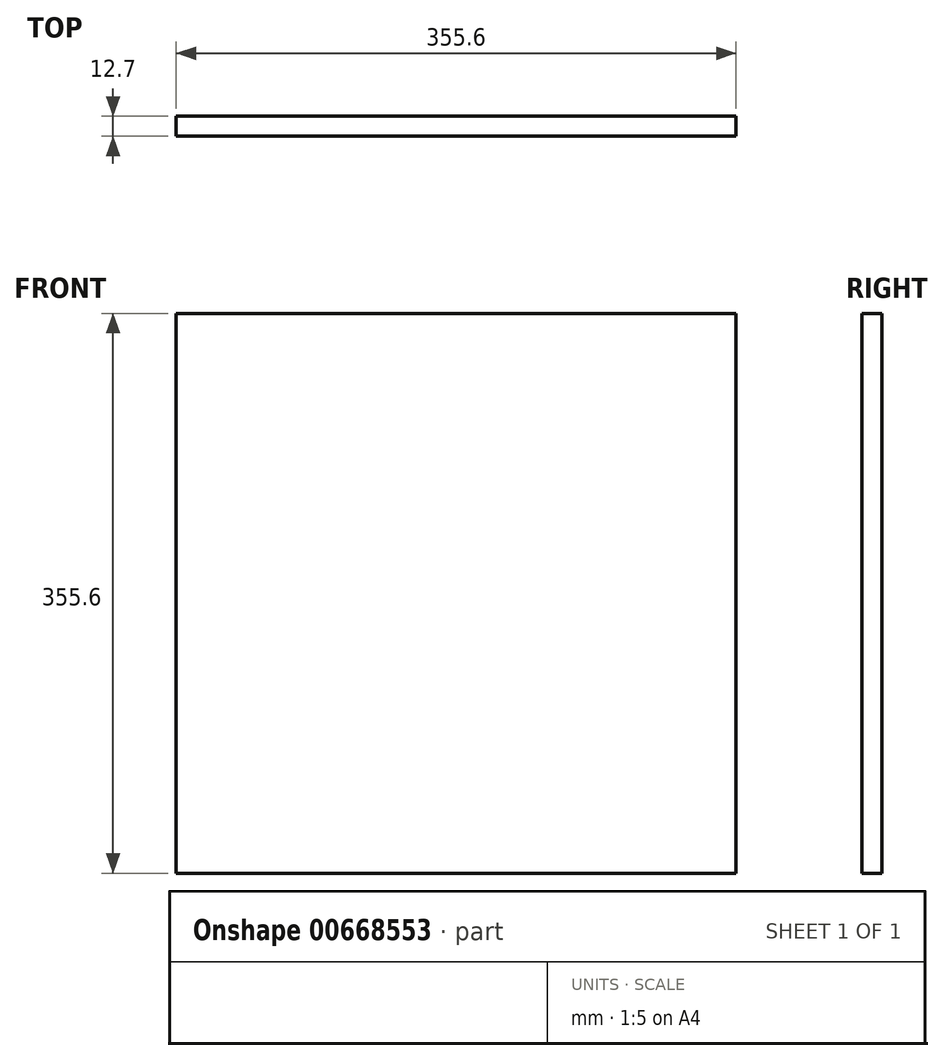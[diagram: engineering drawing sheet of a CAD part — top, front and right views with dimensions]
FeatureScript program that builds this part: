
annotation { "Feature Type Name" : "Feature", "Feature Type Description" : "" }
export const myFeature = defineFeature(function(context is Context, id is Id, definition is map)
    precondition{}
    {
        {
            var Q0;
            Q0=qCreatedBy(makeId("Front.planeOp"),FACE);
            var sketch = newSketch(context, id + "F0", { "sketchPlane" : qUnion([Q0])});
            skLineSegment(sketch, "E0.bottom", {"start": v(180, 177.8) * mm, "end": v(-175.6, 177.8) * mm});
            skLineSegment(sketch, "E0.top", {"start": v(180, -177.8) * mm, "end": v(-175.6, -177.8) * mm});
            skLineSegment(sketch, "E0.left", {"start": v(180, 177.8) * mm, "end": v(180, -177.8) * mm});
            skLineSegment(sketch, "E0.right", {"start": v(-175.6, 177.8) * mm, "end": v(-175.6, -177.8) * mm});
            skPoint(sketch, "E0.middle", {"position": v(2.2, 0) * mm});
            skSolve(sketch);
        }
        {
            var Q0;
            Q0 = qSketchRegion(id + "F0", true);
            extrude(context, id + "F1", {"entities" : qUnion([Q0]), "depth" : 12.7 * mm, "offsetDistance" : 25.4 * mm});
        }
    });
